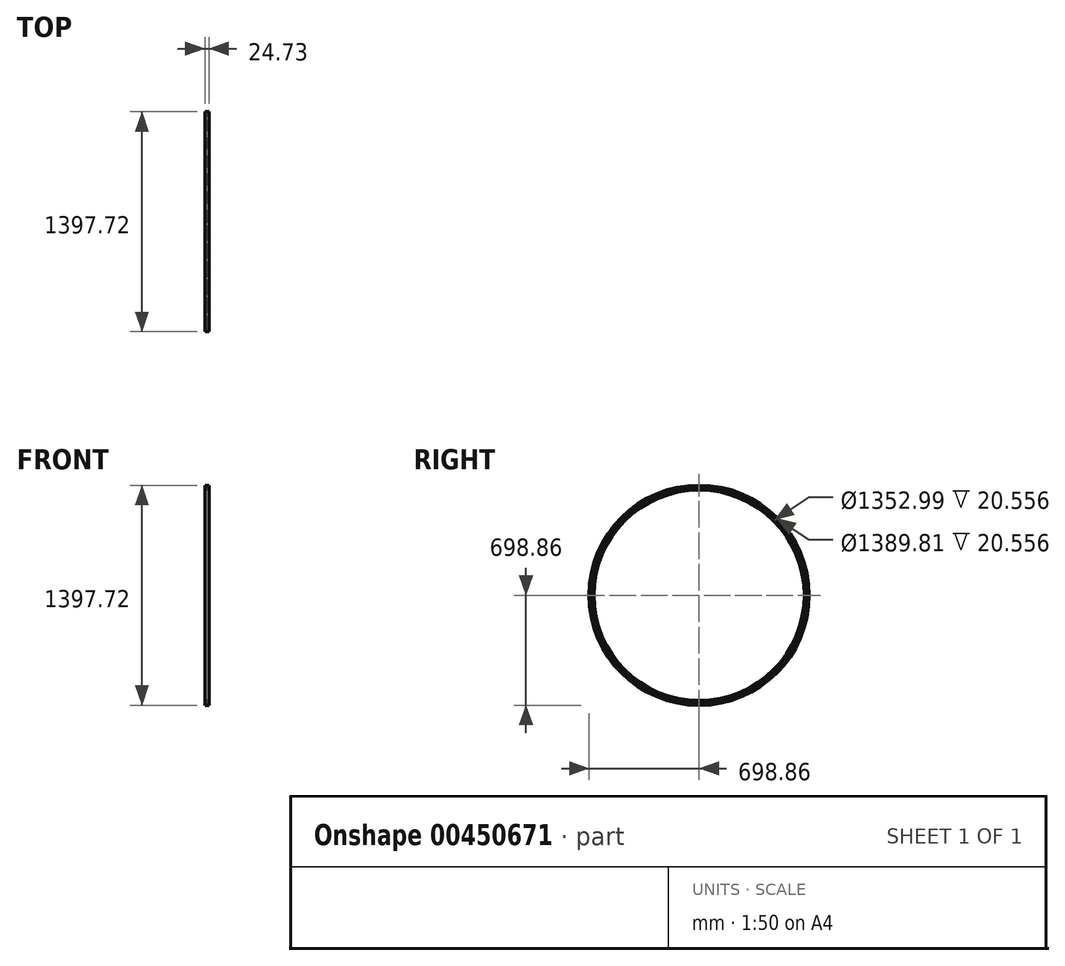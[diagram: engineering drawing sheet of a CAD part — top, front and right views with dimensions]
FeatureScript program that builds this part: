
annotation { "Feature Type Name" : "Feature", "Feature Type Description" : "" }
export const myFeature = defineFeature(function(context is Context, id is Id, definition is map)
    precondition{}
    {
        {
            var Q0;
            Q0=qCreatedBy(makeId("Front.planeOp"),FACE);
            var sketch = newSketch(context, id + "F0", { "sketchPlane" : qUnion([Q0])});
            skLineSegment(sketch, "E0", {"start": v(-27.36, 14.58) * mm, "end": v(-27.36, 10.1) * mm});
            skLineSegment(sketch, "E1", {"start": v(-27.36, 10.1) * mm, "end": v(-6.71, 10.1) * mm});
            skLineSegment(sketch, "E2", {"start": v(-6.71, 10.1) * mm, "end": v(-6.71, 6.63) * mm});
            skLineSegment(sketch, "E3", {"start": v(-6.71, 6.63) * mm, "end": v(-27.27, 6.63) * mm});
            skLineSegment(sketch, "E4", {"start": v(-27.27, 6.63) * mm, "end": v(-27.27, 2.67) * mm});
            skLineSegment(sketch, "E5", {"start": v(-27.27, 2.67) * mm, "end": v(-2.63, 2.67) * mm});
            skLineSegment(sketch, "E6", {"start": v(-2.63, 2.67) * mm, "end": v(-2.63, 14.73) * mm});
            skLineSegment(sketch, "E7", {"start": v(-2.63, 14.73) * mm, "end": v(-27.36, 14.58) * mm});
            skLineSegment(sketch, "E8", {"start": v(-27.36, -3.83) * mm, "end": v(-27.36, -8.3) * mm});
            skLineSegment(sketch, "E9", {"start": v(-27.36, -8.3) * mm, "end": v(-6.71, -8.3) * mm});
            skLineSegment(sketch, "E10", {"start": v(-6.71, -8.3) * mm, "end": v(-6.71, -11.79) * mm});
            skLineSegment(sketch, "E11", {"start": v(-6.71, -11.79) * mm, "end": v(-27.27, -11.79) * mm});
            skLineSegment(sketch, "E12", {"start": v(-27.27, -11.79) * mm, "end": v(-27.27, -15.74) * mm});
            skLineSegment(sketch, "E13", {"start": v(-27.27, -15.74) * mm, "end": v(-2.63, -15.74) * mm});
            skLineSegment(sketch, "E14", {"start": v(-2.63, -15.74) * mm, "end": v(-2.63, -3.69) * mm});
            skLineSegment(sketch, "E15", {"start": v(-2.63, -3.69) * mm, "end": v(-27.36, -3.83) * mm});
            skSolve(sketch);
        }
        {
            var Q0;
            Q0=qCreatedBy(makeId("Front.planeOp"),FACE);
            var sketch = newSketch(context, id + "F1", { "sketchPlane" : qUnion([Q0])});
            skLineSegment(sketch, "E16", {"start": v(-479.74, 683.12) * mm, "end": v(650.23, 683.12) * mm, "construction": true});
            skSolve(sketch);
        }
        {
            var Q0;
            Q0=makeQuery(id+"F0.imprint","IMPRINT",FACE,{"disambiguationData":[TD([[makeQuery(id+"F0.imprint","IMPRINT",EDGE,{"derivedFrom":sQuery(id+"F0.wireOp",EDGE,"E8")}),1.0]])]});
            var Q1;
            Q1=makeQuery(id+"F0.imprint","IMPRINT",FACE,{"disambiguationData":[TD([[makeQuery(id+"F0.imprint","IMPRINT",EDGE,{"derivedFrom":sQuery(id+"F0.wireOp",EDGE,"E0")}),1.0]])]});
            var Q2;
            Q2=sQuery(id+"F1.wireOp",EDGE,"E16");
            revolve(context, id + "F2", {"entities" : qUnion([Q0, Q1]), "axis" : qUnion([Q2]), "revolveType" : RevolveType.FULL});
        }
    });
